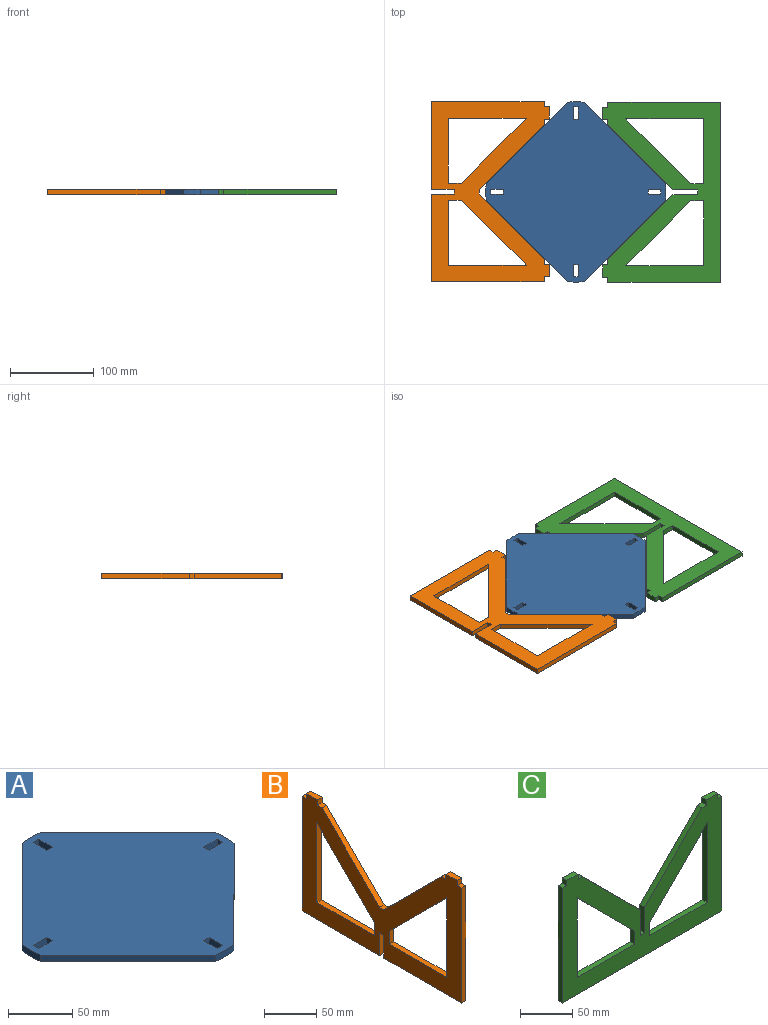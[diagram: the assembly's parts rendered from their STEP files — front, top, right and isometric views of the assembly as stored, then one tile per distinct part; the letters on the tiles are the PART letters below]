
ASSEMBLY  parts=3 mates=4
PART A: 26 faces, bbox 215x215x6 mm
  f0: plane 215x215mm, normal (0,0,1), area 26667.1mm2, adj f1,f2,f3,f4,f5,f6,f7,f8
  f1: plane 97.03x97.03mm, normal (-0.71,0.71,0), area 823.4mm2, adj f0,f2,f8,f9
  f2: cylinder r=107.5mm len=20mm, axis (0,0,1), area 120.2mm2, adj f0,f1,f3,f9
  f3: plane 97.03x97.03mm, normal (0.71,0.71,0), area 823.4mm2, adj f0,f2,f4,f9
  f4: cylinder r=107.5mm len=20mm, axis (0,0,1), area 120.2mm2, adj f0,f3,f5,f9
  f5: plane 97.03x97.03mm, normal (0.71,-0.71,0), area 823.4mm2, adj f0,f4,f6,f9
  f6: cylinder r=107.5mm len=20mm, axis (0,0,1), area 120.2mm2, adj f0,f5,f7,f9
  f7: plane 97.03x97.03mm, normal (-0.71,-0.71,0), area 823.4mm2, adj f0,f6,f8,f9
  f8: cylinder r=107.5mm len=20mm, axis (0,0,1), area 120.2mm2, adj f0,f1,f7,f9
  f9: plane 215x215mm, normal (0,0,-1), area 26667.1mm2, adj f1,f2,f3,f4,f5,f6,f7,f8
  f10: plane 14.9x6mm, normal (-1,0,0), area 89.4mm2, adj f0,f9,f12,f13
  f11: plane 14.9x6mm, normal (1,0,0), area 89.4mm2, adj f0,f9,f12,f13
  f12: plane 6x5.9mm, normal (0,1,0), area 35.4mm2, adj f0,f9,f10,f11
  f13: plane 6x5.9mm, normal (0,-1,0), area 35.4mm2, adj f0,f9,f10,f11
  f14: plane 6x5.9mm, normal (0,1,0), area 35.4mm2, adj f0,f9,f16,f17
  f15: plane 6x5.9mm, normal (0,-1,0), area 35.4mm2, adj f0,f9,f16,f17
  f16: plane 14.9x6mm, normal (1,0,0), area 89.4mm2, adj f0,f9,f14,f15
  f17: plane 14.9x6mm, normal (-1,0,0), area 89.4mm2, adj f0,f9,f14,f15
  f18: plane 14.9x6mm, normal (0,1,0), area 89.4mm2, adj f0,f9,f20,f21
  f19: plane 14.9x6mm, normal (0,-1,0), area 89.4mm2, adj f0,f9,f20,f21
  f20: plane 6x5.9mm, normal (1,0,0), area 35.4mm2, adj f0,f9,f18,f19
  f21: plane 6x5.9mm, normal (-1,0,0), area 35.4mm2, adj f0,f9,f18,f19
  f22: plane 14.9x6mm, normal (0,1,0), area 89.4mm2, adj f0,f9,f24,f25
  f23: plane 14.9x6mm, normal (0,-1,0), area 89.4mm2, adj f0,f9,f24,f25
  f24: plane 6x5.9mm, normal (-1,0,0), area 35.4mm2, adj f0,f9,f22,f23
  f25: plane 6x5.9mm, normal (1,0,0), area 35.4mm2, adj f0,f9,f22,f23
PART B: 30 faces, bbox 6x215x140 mm
  f0: plane 104.6x6mm, normal (0,0,-1), area 627.6mm2, adj f1,f27,f28,f29
  f1: plane 26.75x6mm, normal (0,1,0), area 160.5mm2, adj f0,f2,f28,f29
  f2: plane 6x5.8mm, normal (0,0,-1), area 34.8mm2, adj f1,f3,f28,f29
  f3: plane 26.75x6mm, normal (0,-1,0), area 160.5mm2, adj f2,f4,f28,f29
  f4: plane 104.6x6mm, normal (0,0,-1), area 627.6mm2, adj f3,f5,f28,f29
  f5: plane 134x6mm, normal (0,1,0), area 804mm2, adj f4,f6,f28,f29
  f6: plane 6x6mm, normal (0,0,1), area 36mm2, adj f5,f7,f28,f29
  f7: plane 6x6mm, normal (0,1,0), area 36mm2, adj f6,f8,f28,f29
  f8: plane 15x6mm, normal (0,0,1), area 90mm2, adj f7,f9,f28,f29
  f9: plane 6x6mm, normal (0,-1,0), area 36mm2, adj f8,f10,f28,f29
  f10: plane 6x6mm, normal (0,0,1), area 36mm2, adj f9,f11,f28,f29
  f11: plane 77.6x77.6mm, normal (0,-0.71,0.71), area 658.5mm2, adj f10,f12,f28,f29
  f12: plane 6x5.8mm, normal (0,0,1), area 34.8mm2, adj f11,f13,f28,f29
  f13: plane 77.6x77.6mm, normal (0,0.71,0.71), area 658.5mm2, adj f12,f14,f28,f29
  f14: plane 6x6mm, normal (0,0,1), area 36mm2, adj f13,f15,f28,f29
  f15: plane 6x6mm, normal (0,1,0), area 36mm2, adj f14,f16,f28,f29
  f16: plane 15x6mm, normal (0,0,1), area 90mm2, adj f15,f17,f28,f29
  f17: plane 6x6mm, normal (0,-1,0), area 36mm2, adj f16,f18,f28,f29
  f18: plane 6x6mm, normal (0,0,1), area 36mm2, adj f17,f27,f28,f29
  f19: plane 77.5x6mm, normal (0,0,1), area 465mm2, adj f20,f25,f28,f29
  f20: plane 15.22x6mm, normal (0,1,0), area 91.3mm2, adj f19,f21,f28,f29
  f21: plane 77.5x77.5mm, normal (0,0.71,-0.71), area 657.6mm2, adj f20,f25,f28,f29
  f22: plane 92.72x6mm, normal (0,1,0), area 556.3mm2, adj f23,f26,f28,f29
  f23: plane 77.5x77.5mm, normal (0,-0.71,-0.71), area 657.6mm2, adj f22,f24,f28,f29
  f24: plane 15.22x6mm, normal (0,-1,0), area 91.3mm2, adj f23,f26,f28,f29
  f25: plane 92.72x6mm, normal (0,-1,0), area 556.3mm2, adj f19,f21,f28,f29
  f26: plane 77.5x6mm, normal (0,0,1), area 465mm2, adj f22,f24,f28,f29
  f27: plane 134x6mm, normal (0,-1,0), area 804mm2, adj f0,f18,f28,f29
  f28: plane 215x140mm, normal (1,0,0), area 13998.3mm2, adj f0,f1,f2,f3,f4,f5,f6,f7
  f29: plane 215x140mm, normal (-1,0,0), area 13998.3mm2, adj f0,f1,f2,f3,f4,f5,f6,f7
PART C: 28 faces, bbox 215x6x140 mm
  f0: plane 15.22x6mm, normal (1,0,0), area 91.3mm2, adj f1,f25,f26,f27
  f1: plane 77.5x77.5mm, normal (0.71,0,-0.71), area 657.6mm2, adj f0,f2,f26,f27
  f2: plane 92.72x6mm, normal (-1,0,0), area 556.3mm2, adj f1,f25,f26,f27
  f3: plane 92.72x6mm, normal (1,0,0), area 556.3mm2, adj f4,f23,f26,f27
  f4: plane 77.5x77.5mm, normal (-0.71,0,-0.71), area 657.6mm2, adj f3,f5,f26,f27
  f5: plane 15.22x6mm, normal (-1,0,0), area 91.3mm2, adj f4,f23,f26,f27
  f6: plane 134x6mm, normal (1,0,0), area 804mm2, adj f7,f24,f26,f27
  f7: plane 6x6mm, normal (0,0,1), area 36mm2, adj f6,f8,f26,f27
  f8: plane 6x6mm, normal (1,0,0), area 36mm2, adj f7,f9,f26,f27
  f9: plane 15x6mm, normal (0,0,1), area 90mm2, adj f8,f10,f26,f27
  f10: plane 6x6mm, normal (-1,0,0), area 36mm2, adj f9,f11,f26,f27
  f11: plane 6x6mm, normal (0,0,1), area 36mm2, adj f10,f12,f26,f27
  f12: plane 77.6x77.6mm, normal (-0.71,0,0.71), area 658.5mm2, adj f11,f13,f26,f27
  f13: plane 29.65x6mm, normal (-1,0,0), area 177.9mm2, adj f12,f14,f26,f27
  f14: plane 6x5.8mm, normal (0,0,1), area 34.8mm2, adj f13,f15,f26,f27
  f15: plane 29.65x6mm, normal (1,0,0), area 177.9mm2, adj f14,f16,f26,f27
  f16: plane 77.6x77.6mm, normal (0.71,0,0.71), area 658.5mm2, adj f15,f17,f26,f27
  f17: plane 6x6mm, normal (0,0,1), area 36mm2, adj f16,f18,f26,f27
  f18: plane 6x6mm, normal (1,0,0), area 36mm2, adj f17,f19,f26,f27
  f19: plane 15x6mm, normal (0,0,1), area 90mm2, adj f18,f20,f26,f27
  f20: plane 6x6mm, normal (-1,0,0), area 36mm2, adj f19,f21,f26,f27
  f21: plane 6x6mm, normal (0,0,1), area 36mm2, adj f20,f22,f26,f27
  f22: plane 134x6mm, normal (-1,0,0), area 804mm2, adj f21,f24,f26,f27
  f23: plane 77.5x6mm, normal (0,0,1), area 465mm2, adj f3,f5,f26,f27
  f24: plane 215x6mm, normal (0,0,-1), area 1290mm2, adj f6,f22,f26,f27
  f25: plane 77.5x6mm, normal (0,0,1), area 465mm2, adj f0,f2,f26,f27
  f26: plane 215x140mm, normal (0,-1,0), area 13981.5mm2, adj f0,f1,f2,f3,f4,f5,f6,f7
  f27: plane 215x140mm, normal (0,1,0), area 13981.5mm2, adj f0,f1,f2,f3,f4,f5,f6,f7
PLACE A t=(87.32,42.24,4.73)mm
PLACE B rot(axis=(0,1,0),90deg) t=(-84.63,42.58,141.73)mm
PLACE C rot(axis=(0.58,-0.58,-0.58),120deg) t=(259.53,41.76,141.73)mm
MATE planar C.f27 <-> A.f0  axis (0,0,1) through (200.73,41.76,144.73)mm
MATE planar B.f28 <-> A.f6  axis (0,0,-1) through (-25.55,42.58,138.73)mm
MATE parallel A.f7 <-> B.f13  axis (-0.71,-0.71,0) through (28.8,-16.27,141.73)mm
MATE parallel B.f11 <-> A.f1  axis (0.71,-0.71,0) through (10.57,84.28,141.73)mm
